# Revit family: 2080040(n0300)
name_source: partatom
category: Security Devices
units: mm (PartAtom-declared; Revit-internal decimal feet)

## family parameters
Always vertical = No
Cut with Voids When Loaded = No
Host = Ceiling
OmniClass Number = 23.85.30.14
OmniClass Title = Presence Detection/Registration
Room Calculation Point = No
Shared = Yes

## types (2) — shared parameters
zero-valued in all types: A

## per-type parameters (varying)
- Type 1: CTN=0; EF000008=0 mm  [stored 0 ft]; EF000040=0 mm  [stored 0 ft]; EF000049=0 mm  [stored 0 ft]; EF000194=0; EF000218=0 mm  [stored 0 ft]; EF000551=0 mm  [stored 0 ft]; EF000846=0 mm  [stored 0 ft]; EF000943=0 mm  [stored 0 ft]; EF001322=0 mm  [stored 0 ft]; EF001323=0 mm  [stored 0 ft]; EF003843=0 mm  [stored 0 ft]; EF003882=0; EF004101=0.00°; EF004265=0 mm  [stored 0 ft]; EF006589=0; EF006590=0; EF008011=0 mm  [stored 0 ft]; EF010517=0 mm  [stored 0 ft]; EF010886=0 mm  [stored 0 ft]; EF010945=0 mm  [stored 0 ft]; EF010946=0 mm  [stored 0 ft]; EF012278=0 mm  [stored 0 ft]; EF012569=0; LOG=0; NOCUPEROU=0; PRICEQUANTITY=0; QUANTITYINT=0; QUANTITYMIN=0
- 2080040: ARTICLENO=NB; BOMINFO=LINA; CATALOG=Theben; COO=HU; CTN=90314990; DEEPLINK_PRODUKTSEITE=http://www.theben.de; DESCLONG=Presence detector for ceiling mounting, Circular detection range up to 24 m, DALI master for max. 50 DALI ballasts, 1 light channel DALI broadcast, Easy configuration of DALI groups, 1 pushbutton input, Use of conventional pushbuttons for maximum design freedom, Flexible assignment of pushbuttons to the desired light channel via optional remote control, Operation switching or constant light control with stand-by functionality, Adaptive 1 channel light measurement, Short-time presence; DESCSHORT=DALI presence detector for ceiling mounting; EF000003=EV000383; EF000007=White; EF000008=110 mm  [stored 0.360892 ft]; EF000010=Presence detector; EF000025=false; EF000040=83 mm  [stored 0.27231 ft]; EF000049=110 mm  [stored 0.360892 ft]; EF000124=Screw clamp; EF000139=Untreated; EF000147=false; EF000187=AC; EF000194=3600; EF000218=37 mm  [stored 0.121391 ft]; EF000416=50, 60 Hz; EF000483=false; EF000551=110 mm  [stored 0.360892 ft]; EF000846=48 mm  [stored 0.15748 ft]; EF000943=48 mm  [stored 0.15748 ft]; EF001098=true; EF001099=false; EF001198=false; EF001257=Thermoplast; EF001322=12000 mm; EF001323=12000 mm; EF001731=-15, 50 °C; EF002169=Plastic; EF003429=true; EF003808=false; EF003814=10, 3000 lx; EF003832=false; EF003843=24000 mm; EF003848=true; EF003858=false; EF003863=true; EF003876=true; EF003882=9010; EF003890=false; EF003898=true; EF003904=true; EF003920=false; EF004101=360.00°; EF004265=48 mm  [stored 0.15748 ft]; EF004293=IK04; EF005474=IP54; EF005624=false; EF006243=false; EF006311=false; EF006569=matt; EF006582=0, 360 °; EF006589=10; EF006590=60; EF006644=false; EF007575=true; EF008011=2500 mm  [stored 8.2021 ft]; EF009569=true; EF010517=46 mm  [stored 0.150919 ft]; EF010886=30 mm  [stored 0.0984252 ft]; EF010945=110 mm  [stored 0.360892 ft]; EF010946=65 mm  [stored 0.213255 ft]; EF011072=false; EF011991=false; EF012278=46 mm  [stored 0.150919 ft]; EF012569=38; EF014925=false; EF014926=false; EF014927=false; EF020270=Passive infrared; EF021180=true; EF023790=false; GEBRAUCHSANLEITUNG=http://www.theben.de; INTNO=7612748006348; LINA=2080040; LOG=300; MANUID=2080040; MANUNAME=Theben AG; MANUTYPEDESC=theRonda P360-110 DALI UP WH; Manufacturer=Theben; Model=2080040; NB=2080040(N0300); NBSYN=$MANUID.($SA.$A.$LOG.); NN=theRonda P DALI; NOCUPEROU=1; PRICEQUANTITY=1; PRODUKTDATENBLATT=http://www.theben.de; QUANTITYINT=1; QUANTITYMIN=1; REACH_ERKLAERUNG=http://www.theben.de; REMARKS=ERP-GROUP 345; SA=None; SUPPLIER=THEBEN; SUPPLIERALTNO=2080040

note: [stored X ft] marks values corroborated as IEEE doubles in the binary element streams (Revit-internal decimal feet)

## geometry (parser evidence)
native form markers: Sweep x13
no freeform markers — native parametric forms only
